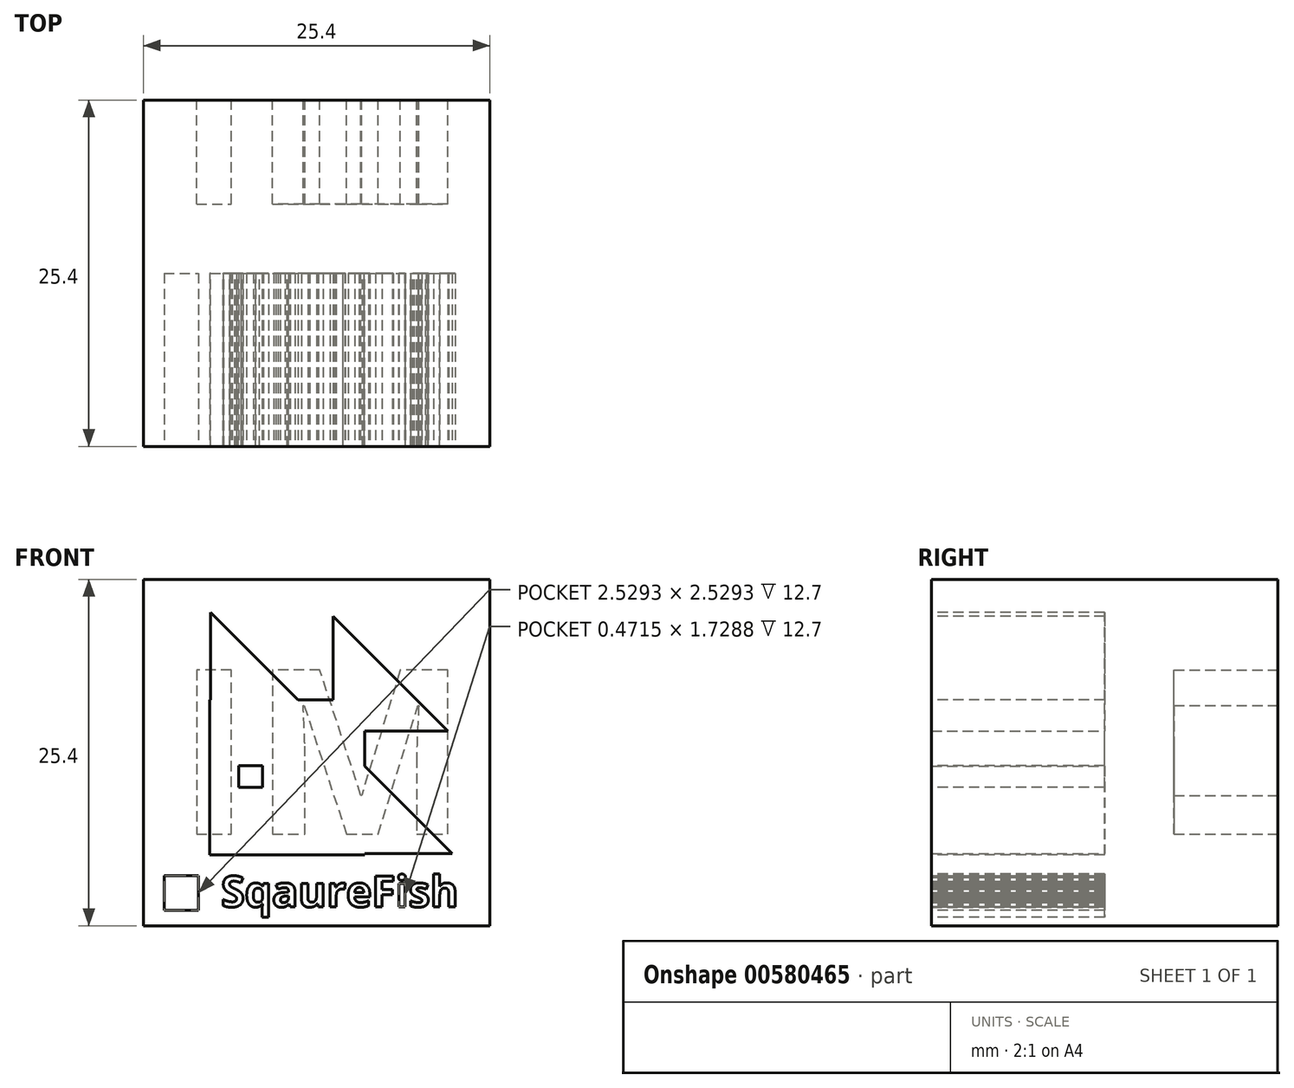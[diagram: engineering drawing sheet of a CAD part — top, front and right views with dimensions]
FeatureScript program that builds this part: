
annotation { "Feature Type Name" : "Feature", "Feature Type Description" : "" }
export const myFeature = defineFeature(function(context is Context, id is Id, definition is map)
    precondition{}
    {
        {
            var Q0;
            Q0=qCreatedBy(makeId("Front.planeOp"),FACE);
            var sketch = newSketch(context, id + "F0", { "sketchPlane" : qUnion([Q0])});
            skLineSegment(sketch, "E0.bottom", {"start": v(12.7, 12.7) * mm, "end": v(-12.7, 12.7) * mm});
            skLineSegment(sketch, "E0.top", {"start": v(12.7, -12.7) * mm, "end": v(-12.7, -12.7) * mm});
            skLineSegment(sketch, "E0.left", {"start": v(12.7, 12.7) * mm, "end": v(12.7, -12.7) * mm});
            skLineSegment(sketch, "E0.right", {"start": v(-12.7, 12.7) * mm, "end": v(-12.7, -12.7) * mm});
            skPoint(sketch, "E0.middle", {"position": v(0, 0) * mm});
            skSolve(sketch);
        }
        {
            var Q0;
            Q0 = qSketchRegion(id + "F0", true);
            extrude(context, id + "F1", {"entities" : qUnion([Q0]), "oppositeDirection" : true, "depth" : 25.4 * mm, "offsetDistance" : 25.4 * mm});
        }
        {
            var Q0;
            Q0=qCreatedBy(makeId("Front.planeOp"),FACE);
            var sketch = newSketch(context, id + "F2", { "sketchPlane" : qUnion([Q0])});
            skLineSegment(sketch, "E1.bottom", {"start": v(-7.84, -7.5) * mm, "end": v(3.51, -7.5) * mm});
            skLineSegment(sketch, "E1.top", {"start": v(-7.84, 3.85) * mm, "end": v(3.51, 3.85) * mm});
            skLineSegment(sketch, "E1.left", {"start": v(-7.84, -7.5) * mm, "end": v(-7.84, 3.85) * mm});
            skLineSegment(sketch, "E1.right", {"start": v(3.51, -7.5) * mm, "end": v(3.51, 3.85) * mm});
            skLineSegment(sketch, "E2.bottom", {"start": v(-7.84, 3.85) * mm, "end": v(-1.22, 3.85) * mm});
            skLineSegment(sketch, "E3.left", {"start": v(3.51, -7.5) * mm, "end": v(3.51, -0.89) * mm});
            skSolve(sketch);
        }
        {
            var Q0;
            Q0 = qSketchRegion(id + "F2", true);
            extrude(context, id + "F3", {"entities" : qUnion([Q0]), "operationType" : NewBodyOperationType.REMOVE, "oppositeDirection" : true, "depth" : 12.7 * mm, "offsetDistance" : 25.4 * mm});
        }
        {
            var Q0;
            Q0=qCreatedBy(makeId("Front.planeOp"),FACE);
            var sketch = newSketch(context, id + "F4", { "sketchPlane" : qUnion([Q0])});
            skLineSegment(sketch, "E4.bottom", {"start": v(-7.8, 3.85) * mm, "end": v(-1.36, 3.85) * mm});
            skLineSegment(sketch, "E4.left", {"start": v(-7.8, 3.85) * mm, "end": v(-7.8, 10.28) * mm});
            skLineSegment(sketch, "E5", {"start": v(-7.8, 10.28) * mm, "end": v(-1.36, 3.85) * mm});
            skSolve(sketch);
        }
        {
            var Q0;
            Q0 = qSketchRegion(id + "F4", true);
            extrude(context, id + "F5", {"entities" : qUnion([Q0]), "operationType" : NewBodyOperationType.REMOVE, "oppositeDirection" : true, "depth" : 12.7 * mm, "offsetDistance" : 25.4 * mm});
        }
        {
            var Q0;
            Q0=qCreatedBy(makeId("Front.planeOp"),FACE);
            var sketch = newSketch(context, id + "F6", { "sketchPlane" : qUnion([Q0])});
            skLineSegment(sketch, "E6.bottom", {"start": v(3.5, -7.42) * mm, "end": v(9.94, -7.42) * mm});
            skLineSegment(sketch, "E6.left", {"start": v(3.5, -7.42) * mm, "end": v(3.5, -1) * mm});
            skLineSegment(sketch, "E7", {"start": v(3.5, -1) * mm, "end": v(9.94, -7.42) * mm});
            skSolve(sketch);
        }
        {
            var Q0;
            Q0 = qSketchRegion(id + "F6", true);
            extrude(context, id + "F7", {"entities" : qUnion([Q0]), "operationType" : NewBodyOperationType.REMOVE, "oppositeDirection" : true, "depth" : 12.7 * mm, "offsetDistance" : 25.4 * mm});
        }
        {
            var Q0;
            Q0=qCreatedBy(makeId("Front.planeOp"),FACE);
            var sketch = newSketch(context, id + "F8", { "sketchPlane" : qUnion([Q0])});
            skLineSegment(sketch, "E8.bottom", {"start": v(1.2, 1.58) * mm, "end": v(9.63, 1.58) * mm});
            skLineSegment(sketch, "E8.left", {"start": v(1.2, 1.58) * mm, "end": v(1.2, 10) * mm});
            skLineSegment(sketch, "E9", {"start": v(1.2, 10) * mm, "end": v(9.63, 1.58) * mm});
            skSolve(sketch);
        }
        {
            var Q0;
            Q0 = qSketchRegion(id + "F8", true);
            extrude(context, id + "F9", {"entities" : qUnion([Q0]), "operationType" : NewBodyOperationType.REMOVE, "oppositeDirection" : true, "depth" : 12.7 * mm, "offsetDistance" : 25.4 * mm});
        }
        {
            var Q0;
            Q0=qCreatedBy(makeId("Front.planeOp"),FACE);
            var sketch = newSketch(context, id + "F10", { "sketchPlane" : qUnion([Q0])});
            skLineSegment(sketch, "E10.bottom", {"start": v(-5.71, -2.56) * mm, "end": v(-3.99, -2.56) * mm});
            skLineSegment(sketch, "E10.top", {"start": v(-5.71, -0.98) * mm, "end": v(-3.99, -0.98) * mm});
            skLineSegment(sketch, "E10.left", {"start": v(-5.71, -2.56) * mm, "end": v(-5.71, -0.98) * mm});
            skLineSegment(sketch, "E10.right", {"start": v(-3.99, -2.56) * mm, "end": v(-3.99, -0.98) * mm});
            skSolve(sketch);
        }
        {
            var Q0;
            Q0 = qSketchRegion(id + "F10", true);
            extrude(context, id + "F11", {"entities" : qUnion([Q0]), "operationType" : NewBodyOperationType.ADD, "oppositeDirection" : true, "depth" : 12.7 * mm, "offsetDistance" : 25.4 * mm});
        }
        {
            var Q0;
            Q0=qCreatedBy(makeId("Front.planeOp"),FACE);
            var sketch = newSketch(context, id + "F12", { "sketchPlane" : qUnion([Q0])});
            skLineSegment(sketch, "E11.bottom", {"start": v(-11.2, -9.04) * mm, "end": v(-8.66, -9.04) * mm});
            skLineSegment(sketch, "E11.top", {"start": v(-11.2, -11.57) * mm, "end": v(-8.66, -11.57) * mm});
            skLineSegment(sketch, "E11.left", {"start": v(-11.2, -9.04) * mm, "end": v(-11.2, -11.57) * mm});
            skLineSegment(sketch, "E11.right", {"start": v(-8.66, -9.04) * mm, "end": v(-8.66, -11.57) * mm});
            skSolve(sketch);
        }
        {
            var Q0;
            Q0 = qSketchRegion(id + "F12", true);
            extrude(context, id + "F13", {"entities" : qUnion([Q0]), "operationType" : NewBodyOperationType.REMOVE, "oppositeDirection" : true, "depth" : 12.7 * mm, "offsetDistance" : 25.4 * mm});
        }
        {
            var Q0;
            Q0=qCreatedBy(makeId("Front.planeOp"),FACE);
            var sketch = newSketch(context, id + "F14", { "sketchPlane" : qUnion([Q0])});
            skText(sketch, "E12", { "text": "SqaureFish", "fontName": "OpenSans-Bold.ttf"});
            const initialGuessF14  = {"E12": [-0.00702, -0.01132, 1, 0, 0.00228]};
            skSetInitialGuess(sketch, initialGuessF14);
            skSolve(sketch);
        }
        {
            var Q0;
            Q0 = qSketchRegion(id + "F14", true);
            extrude(context, id + "F15", {"entities" : qUnion([Q0]), "operationType" : NewBodyOperationType.REMOVE, "oppositeDirection" : true, "depth" : 12.7 * mm, "offsetDistance" : 25.4 * mm});
        }
        {
            var Q0;
            Q0=makeQuery(id+"F1.opExtrude","CAP_FACE",FACE,{"disambiguationData":[OSD([sQuery(id+"F0.wireOp",EDGE,"E0.bottom"),sQuery(id+"F0.wireOp",EDGE,"E0.top"),sQuery(id+"F0.wireOp",EDGE,"E0.left"),sQuery(id+"F0.wireOp",EDGE,"E0.right")])],"isStart":false});
            var sketch = newSketch(context, id + "F16", { "sketchPlane" : qUnion([Q0])});
            skText(sketch, "E13", { "text": "MI", "fontName": "OpenSans-Bold.ttf"});
            const initialGuessF16  = {"E13": [-0.01112, -0.00597, 1, 0, 0.01212]};
            skSetInitialGuess(sketch, initialGuessF16);
            skSolve(sketch);
        }
        {
            var Q0;
            Q0 = qSketchRegion(id + "F16", true);
            extrude(context, id + "F17", {"entities" : qUnion([Q0]), "operationType" : NewBodyOperationType.REMOVE, "oppositeDirection" : true, "depth" : 7.62 * mm, "offsetDistance" : 25.4 * mm});
        }
    });
